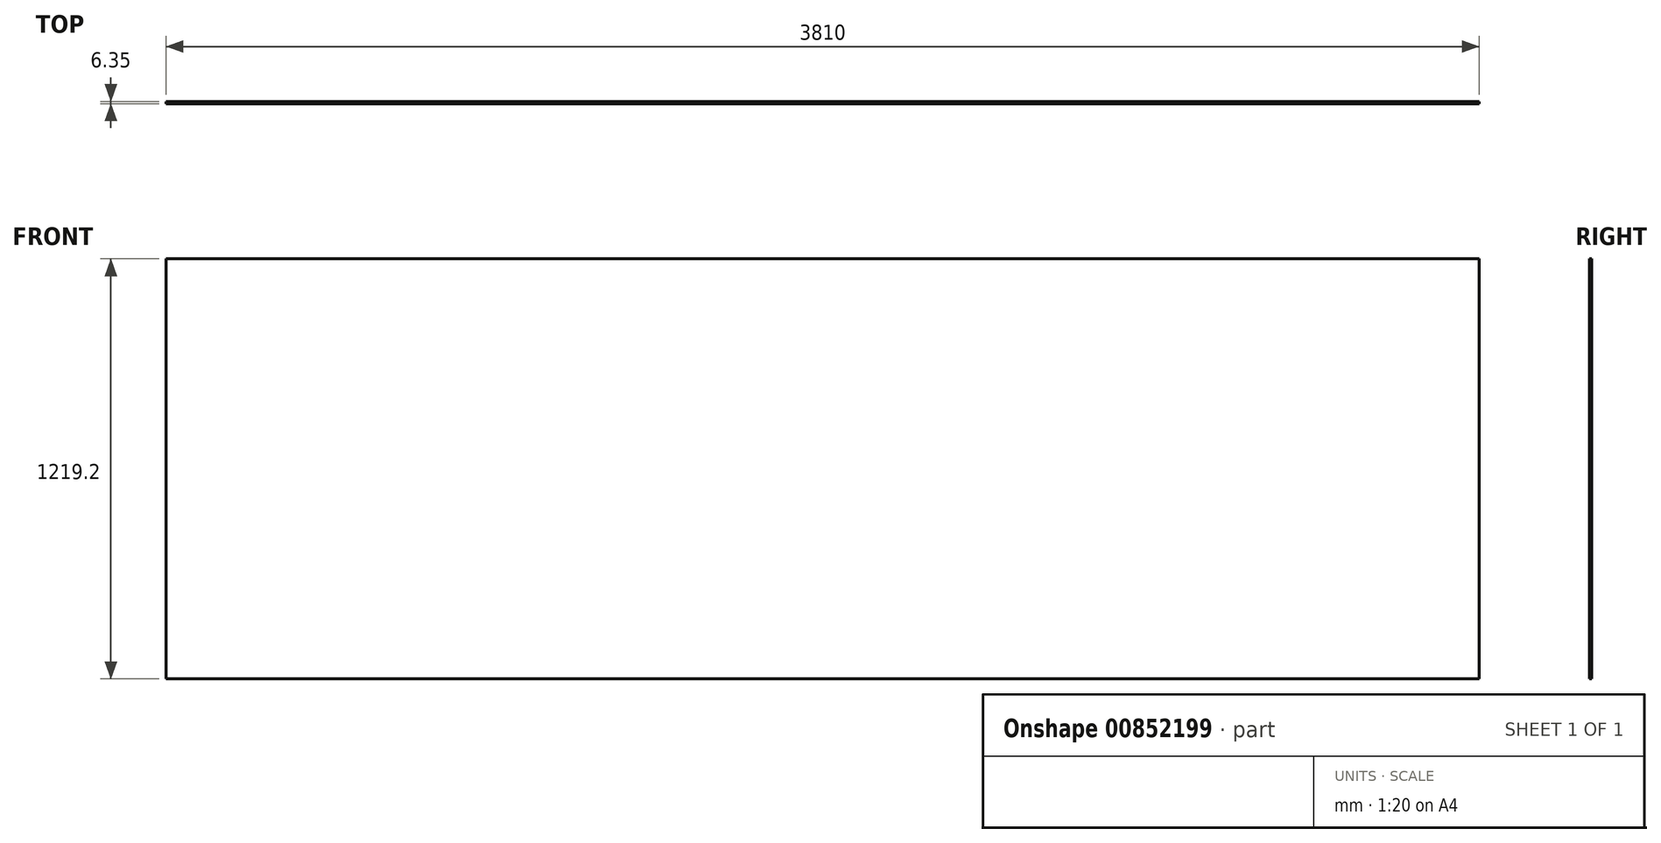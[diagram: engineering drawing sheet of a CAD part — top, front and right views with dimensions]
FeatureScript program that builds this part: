
annotation { "Feature Type Name" : "Feature", "Feature Type Description" : "" }
export const myFeature = defineFeature(function(context is Context, id is Id, definition is map)
    precondition{}
    {
        {
            var Q0;
            Q0=qCreatedBy(makeId("Front.planeOp"),FACE);
            var sketch = newSketch(context, id + "F0", { "sketchPlane" : qUnion([Q0])});
            skLineSegment(sketch, "E0.bottom", {"start": v(1905, -612.7) * mm, "end": v(-1905, -612.7) * mm});
            skLineSegment(sketch, "E0.top", {"start": v(1905, 606.5) * mm, "end": v(-1905, 606.5) * mm});
            skLineSegment(sketch, "E0.left", {"start": v(1905, -612.7) * mm, "end": v(1905, 606.5) * mm});
            skLineSegment(sketch, "E0.right", {"start": v(-1905, -612.7) * mm, "end": v(-1905, 606.5) * mm});
            skPoint(sketch, "E0.middle", {"position": v(0, -3.1) * mm});
            skSolve(sketch);
        }
        {
            var Q0;
            Q0=qSketchRegion(id+"F0",true);
            extrude(context, id + "F1", {"entities" : qUnion([Q0]), "depth" : 6.35 * mm, "offsetDistance" : 25.4 * mm});
        }
    });
